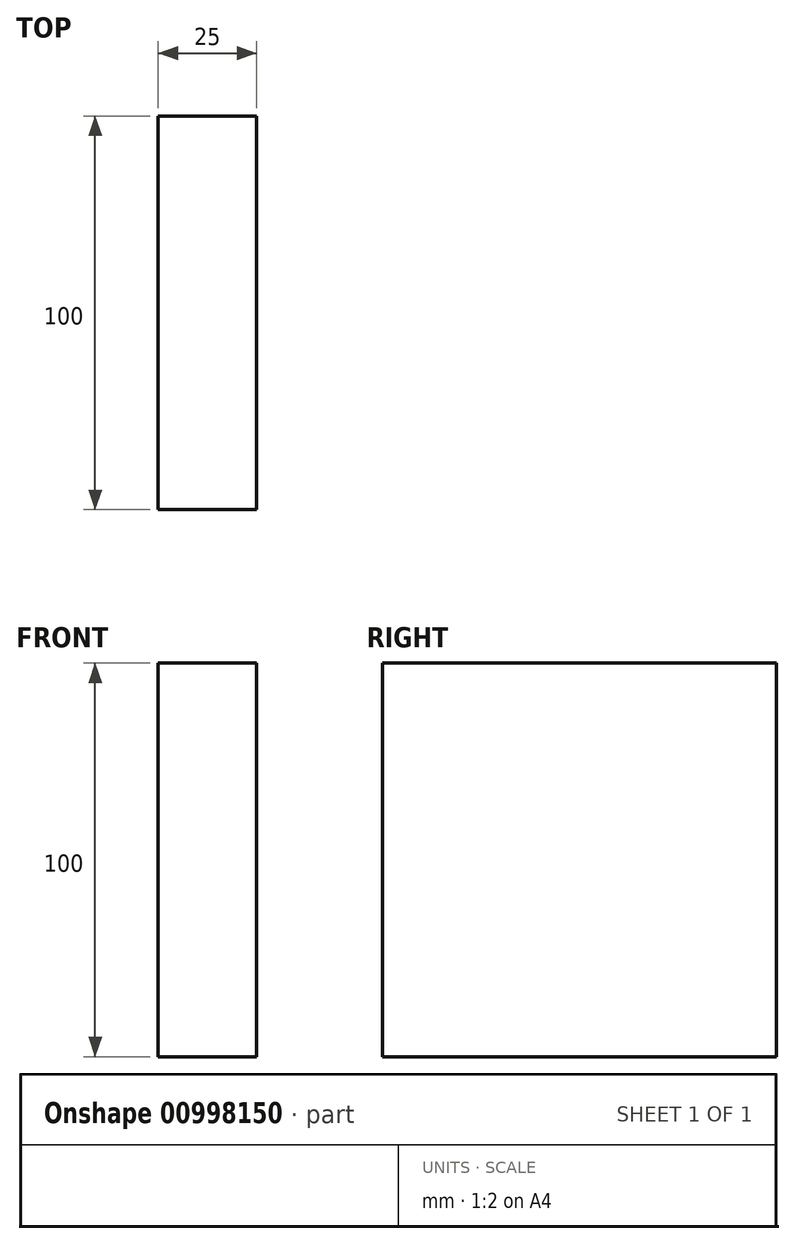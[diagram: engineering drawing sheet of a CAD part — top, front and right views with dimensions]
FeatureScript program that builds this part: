
annotation { "Feature Type Name" : "Feature", "Feature Type Description" : "" }
export const myFeature = defineFeature(function(context is Context, id is Id, definition is map)
    precondition{}
    {
        {
            var Q0;
            Q0=qCreatedBy(makeId("Right.planeOp"),FACE);
            var sketch = newSketch(context, id + "F0", { "sketchPlane" : qUnion([Q0])});
            skLineSegment(sketch, "E0.bottom", {"start": v(50, 50) * mm, "end": v(-50, 50) * mm});
            skLineSegment(sketch, "E0.top", {"start": v(50, -50) * mm, "end": v(-50, -50) * mm});
            skLineSegment(sketch, "E0.left", {"start": v(50, 50) * mm, "end": v(50, -50) * mm});
            skLineSegment(sketch, "E0.right", {"start": v(-50, 50) * mm, "end": v(-50, -50) * mm});
            skPoint(sketch, "E0.middle", {"position": v(0, 0) * mm});
            skSolve(sketch);
        }
        {
            var Q0;
            Q0 = qSketchRegion(id + "F0", true);
            extrude(context, id + "F1", {"entities" : qUnion([Q0]), "depth" : 25 * mm, "offsetDistance" : 25 * mm});
        }
    });
